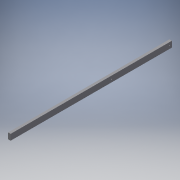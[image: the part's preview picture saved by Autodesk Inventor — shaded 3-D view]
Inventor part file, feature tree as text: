
AUTODESK INVENTOR PART (.ipt)
format: ipt  version: 2019 (Build 230136000, 136)  size: 110,080 bytes
history: native  units: in
note: dims shown in document units (in); Inventor stores cm internally (conversion verified against a paired STEP export)
features: extrude x2, sketch x2
ambient origin geometry x8: Origin, YZ Plane, XZ Plane, XY Plane, X Axis, Y Axis, Z Axis, Center Point
bodies: Solid1 (feature_tree)
feature tree (4):
  extrude  "Extrusion1"  Depth=96.0in
  extrude  "Extrusion2"  Depth=1.5in
  sketch  "Sketch1"  dims[d0=3.5in d1=96.0in]
  sketch  "Sketch2"  dims[d2=3.5in d3=1.5in d4=0.5in d5=1.5in d6=0.0in d7=34.5in d8=0.5in d9=1.5in d10=0.0in]
